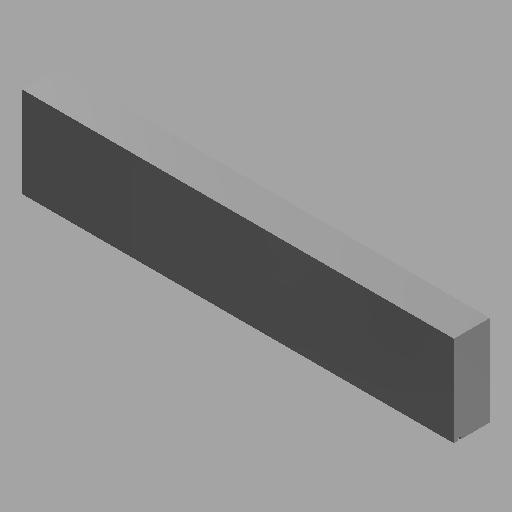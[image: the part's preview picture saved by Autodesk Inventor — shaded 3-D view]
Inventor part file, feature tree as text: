
AUTODESK INVENTOR PART (.ipt)
format: ipt  version: 2023 (Build 270158030, 158C)  size: 100,352 bytes
history: native  units: mm (DEFAULTED — no unit token found)
features: extrude x2, sketch x2
ambient origin geometry x8: Origin, YZ Plane, XZ Plane, XY Plane, X Axis, Y Axis, Z Axis, Center Point
bodies: Solid1 (feature_tree)
feature tree (4):
  extrude  "Extrusion1"  Depth=25.4mm TaperAngle=0.0deg
  extrude  "Extrusion2"  [1 undecoded]
  sketch  "Sketch1"  dims[d0=25.4mm d1=0.0mm d2=25.4mm d3=0.0mm]
  sketch  "Sketch2"
note: 1 required parameter value undecoded (feature->parameter linkage not recoverable at this tier; creation-order binding heuristic only, values carry confidence <= 0.55)
